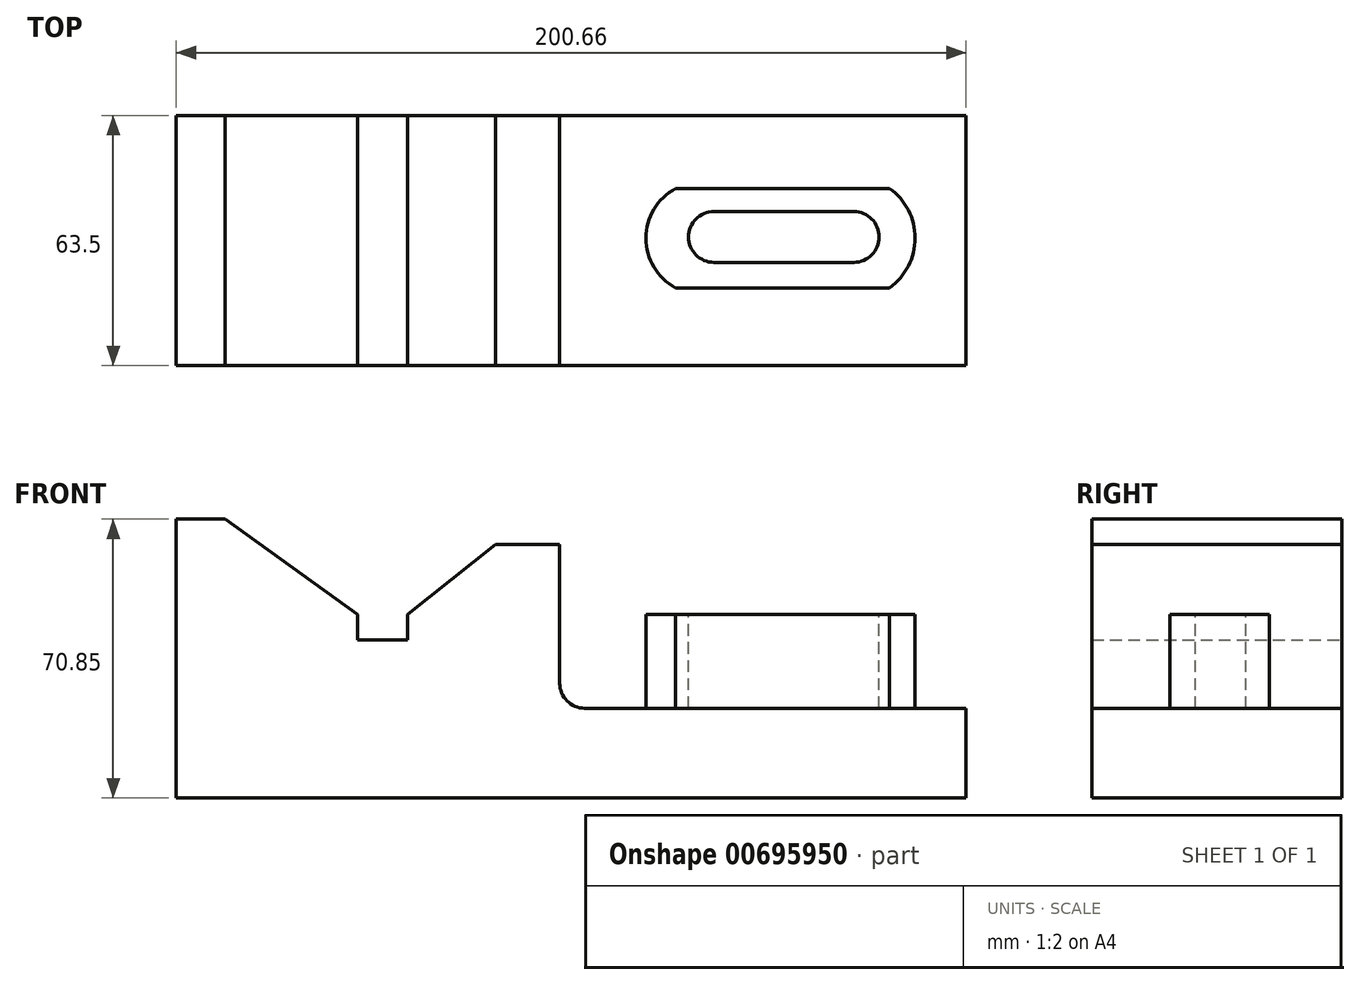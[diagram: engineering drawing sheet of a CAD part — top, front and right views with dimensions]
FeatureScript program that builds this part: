
annotation { "Feature Type Name" : "Feature", "Feature Type Description" : "" }
export const myFeature = defineFeature(function(context is Context, id is Id, definition is map)
    precondition{}
    {
        {
            var Q0;
            Q0=qCreatedBy(makeId("Front.planeOp"),FACE);
            var sketch = newSketch(context, id + "F0", { "sketchPlane" : qUnion([Q0])});
            skLineSegment(sketch, "E0", {"start": v(-97.85, -46.57) * mm, "end": v(102.8, -46.57) * mm});
            skLineSegment(sketch, "E1", {"start": v(102.8, -46.57) * mm, "end": v(102.8, -23.78) * mm});
            skLineSegment(sketch, "E2", {"start": v(102.8, -23.78) * mm, "end": v(5.92, -23.78) * mm});
            skLineSegment(sketch, "E3", {"start": v(-0.43, -17.43) * mm, "end": v(-0.43, 17.84) * mm});
            skLineSegment(sketch, "E4", {"start": v(-0.43, 17.84) * mm, "end": v(-16.78, 17.84) * mm});
            skLineSegment(sketch, "E5", {"start": v(-16.78, 17.84) * mm, "end": v(-39.08, 0) * mm});
            skLineSegment(sketch, "E6", {"start": v(-39.08, 0) * mm, "end": v(-39.08, -6.44) * mm});
            skLineSegment(sketch, "E7", {"start": v(-39.08, -6.44) * mm, "end": v(-51.78, -6.44) * mm});
            skLineSegment(sketch, "E8", {"start": v(-51.78, -6.44) * mm, "end": v(-51.78, 0) * mm});
            skLineSegment(sketch, "E9", {"start": v(-51.78, 0) * mm, "end": v(-85.47, 24.28) * mm});
            skLineSegment(sketch, "E10", {"start": v(-85.47, 24.28) * mm, "end": v(-97.85, 24.28) * mm});
            skLineSegment(sketch, "E11", {"start": v(-97.85, 24.28) * mm, "end": v(-97.85, -46.57) * mm});
            skPoint(sketch, "E12.visualSharp", {"position": v(-0.43, -23.78) * mm});
            skArc(sketch, "E12.filletArc", {"start": v(-0.43, -17.43) * mm, "mid": v(1.43, -21.92) * mm, "end": v(5.92, -23.78) * mm});
            skSolve(sketch);
        }
        {
            var Q0;
            Q0 = qSketchRegion(id + "F0", true);
            extrude(context, id + "F1", {"entities" : qUnion([Q0]), "depth" : 63.5 * mm, "offsetDistance" : 25.4 * mm});
        }
        {
            var Q0;
            Q0=qCreatedBy(makeId("Top.planeOp"),FACE);
            var sketch = newSketch(context, id + "F2", { "sketchPlane" : qUnion([Q0])});
            skLineSegment(sketch, "E13.bottom", {"start": v(29.05, -18.5) * mm, "end": v(83.37, -18.5) * mm});
            skLineSegment(sketch, "E13.top", {"start": v(29.05, -43.75) * mm, "end": v(83.37, -43.75) * mm});
            skArc(sketch, "E14", {"start": v(83.37, -43.75) * mm, "mid": v(89.85, -31.12) * mm, "end": v(83.37, -18.5) * mm});
            skArc(sketch, "E15", {"start": v(29.05, -18.5) * mm, "mid": v(21.48, -31.12) * mm, "end": v(29.05, -43.75) * mm});
            skLineSegment(sketch, "E16.bottom", {"start": v(38.74, -24.37) * mm, "end": v(74.27, -24.37) * mm});
            skLineSegment(sketch, "E16.top", {"start": v(38.74, -37.29) * mm, "end": v(74.27, -37.29) * mm});
            skArc(sketch, "E17", {"start": v(38.74, -24.37) * mm, "mid": v(32.28, -30.83) * mm, "end": v(38.74, -37.29) * mm});
            skArc(sketch, "E18", {"start": v(74.27, -37.29) * mm, "mid": v(80.73, -30.83) * mm, "end": v(74.27, -24.37) * mm});
            skSolve(sketch);
        }
        {
            var Q0;
            Q0 = qSketchRegion(id + "F2", true);
            extrude(context, id + "F3", {"entities" : qUnion([Q0]), "operationType" : NewBodyOperationType.ADD, "oppositeDirection" : true, "depth" : 25.4 * mm, "offsetDistance" : 25.4 * mm});
        }
    });
